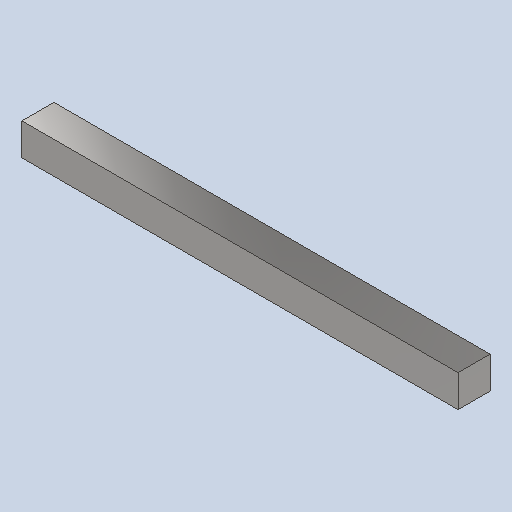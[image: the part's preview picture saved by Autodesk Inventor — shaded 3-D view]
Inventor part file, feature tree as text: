
AUTODESK INVENTOR PART (.ipt)
format: ipt  version: 2024 (Build 280153000, 153)  size: 86,528 bytes
history: native  units: in
note: dims shown in document units (in); Inventor stores cm internally (conversion verified against a paired STEP export)
features: other x3, sketch x1
ambient origin geometry x8: Origin, YZ Plane, XZ Plane, XY Plane, X Axis, Y Axis, Z Axis, Center Point
bodies: Solid1 (feature_tree)
feature tree (4):
  other  "Steelbar.ipt"
  other  "Solid1::Steelbar.ipt"
  other  "TaggingFeature1"
  sketch  "Sketch1"  dims[d0=0.3937in]
